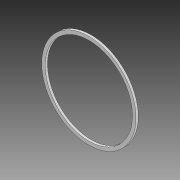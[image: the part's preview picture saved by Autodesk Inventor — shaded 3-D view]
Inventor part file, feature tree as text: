
AUTODESK INVENTOR PART (.ipt)
format: ipt  version: 2020 (Build 240168000, 168)  size: 84,992 bytes
history: native  units: mm
features: extrude x1, sketch x1
ambient origin geometry x8: Origin, YZ Plane, XZ Plane, XY Plane, X Axis, Y Axis, Z Axis, Center Point
bodies: Body1 (feature_tree)
feature tree (2):
  extrude  "Extrusion1"  Depth=2.0mm
  sketch  "Sketch2"  dims[d7=75.5mm d8=3.0mm d9=2.0mm d10=0.0mm]
